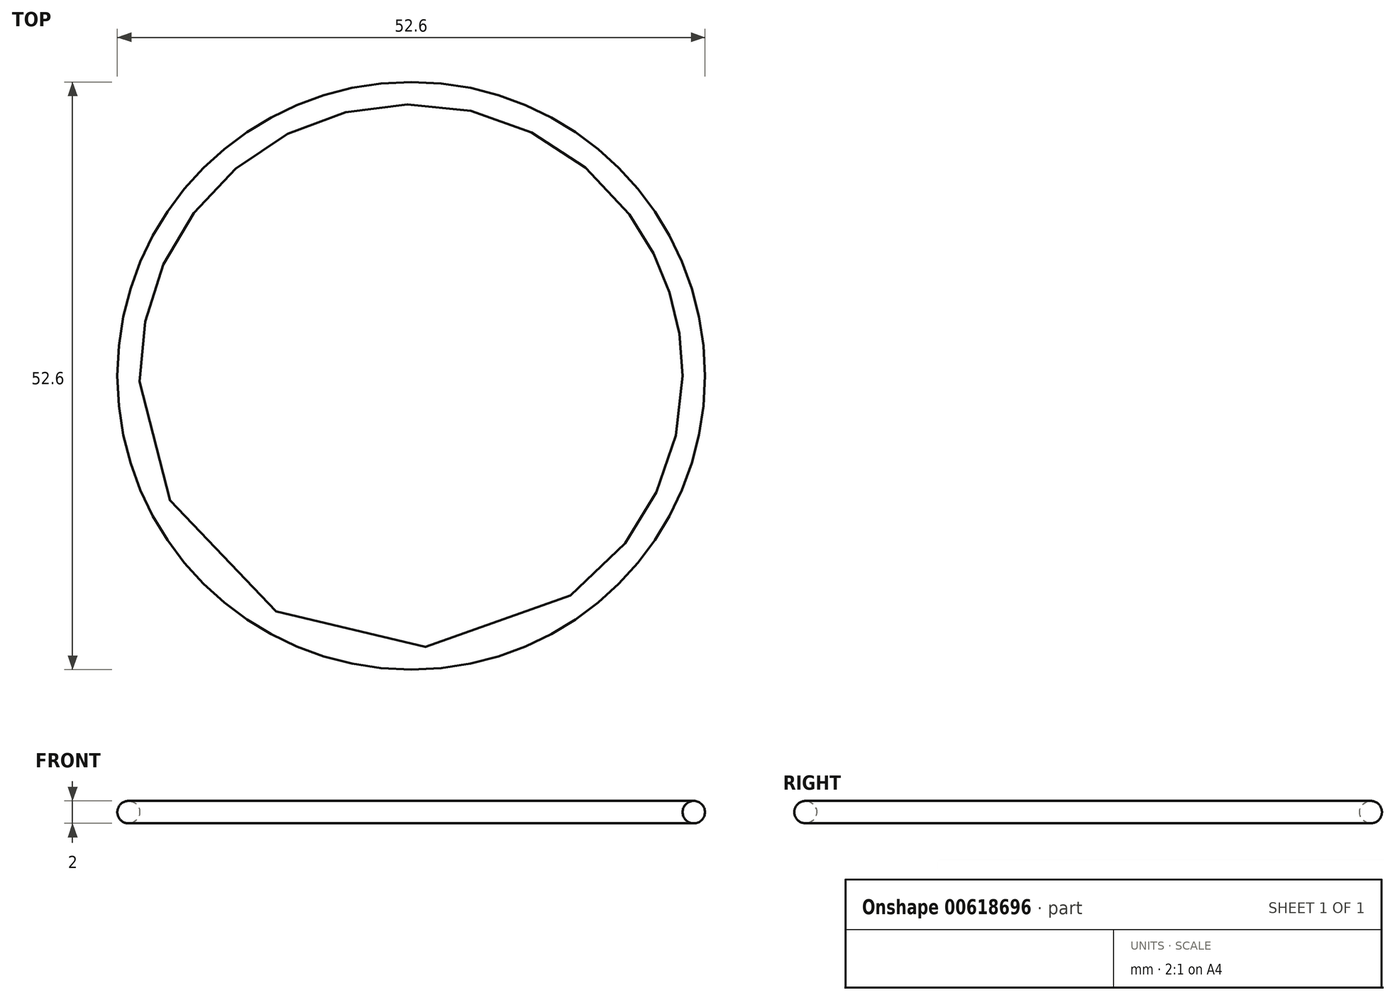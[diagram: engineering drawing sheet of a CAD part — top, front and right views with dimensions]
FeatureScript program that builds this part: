
annotation { "Feature Type Name" : "Feature", "Feature Type Description" : "" }
export const myFeature = defineFeature(function(context is Context, id is Id, definition is map)
    precondition{}
    {
        {
            var Q0;
            Q0=qCreatedBy(makeId("Front.planeOp"),FACE);
            var sketch = newSketch(context, id + "F0", { "sketchPlane" : qUnion([Q0])});
            skCircle(sketch, "E0", {"center": v(-25.3, 0) * mm, "radius": 1 * mm});
            skSolve(sketch);
        }
        {
            var Q0;
            Q0=qCreatedBy(makeId("Front.planeOp"),FACE);
            var sketch = newSketch(context, id + "F1", { "sketchPlane" : qUnion([Q0])});
            skLineSegment(sketch, "E1", {"start": v(0, 27.83) * mm, "end": v(0, -27.34) * mm, "construction": true});
            skSolve(sketch);
        }
        {
            var Q0;
            Q0=makeQuery(id+"F0.imprint","IMPRINT",FACE,{"disambiguationData":[TD([[makeQuery(id+"F0.imprint","IMPRINT",EDGE,{"derivedFrom":sQuery(id+"F0.wireOp",EDGE,"E0")}),1.0]])]});
            var Q1;
            Q1=sQuery(id+"F1.wireOp",EDGE,"E1");
            revolve(context, id + "F2", {"surfaceOperationType" : NewSurfaceOperationType.NEW, "entities" : qUnion([Q0]), "axis" : qUnion([Q1]), "revolveType" : RevolveType.FULL});
        }
    });
